# Revit family: S-776
name_source: partatom
category: Aparatos sanitarios
revit_build: Autodesk Revit 2015 (Build: 20140606_1530(x64)
units: mm (PartAtom-declared; Revit-internal decimal feet)

## types (6) — shared parameters
B = 72 mm
Comentarios de tipo = COMPATIBLE CON CERCOS VISTOS Y OCULTOS
Descripción = REJILLA PARA CANALETA, SEQUENCE, PARA CANALETAS ANCHO 70
DistExt = 15 mm  [stored 0.0492126 ft]
Fabricante = Jimten
Material = INOX AISI304
Modelo = S-776
Rejilla = INOX AISI304
URL = http://www.jimten.com

## per-type parameters (varying)
| type | A | Medida | N_MatrizHuecos | Referencia |
| 70x350mm_SEQUENCE | 340 mm | 350mm x 70mm | 3 | 13739 |
| 70x550mm_SEQUENCE | 540 mm  [stored 1.77165 ft] | 550mm x 70mm | 5 | 13759 |
| 70x650mm_SEQUENCE | 640 mm  [stored 2.09974 ft] | 650mm x 70mm | 6 | 13769 |
| 70x750mm_SEQUENCE | 740 mm | 750mm x 70mm | 7 | 13779 |
| 70x850mm_SEQUENCE | 840 mm | 850mm x 70mm | 8 | 13789 |
| 70x950mm_SEQUENCE | 940 mm | 950mm x 70mm | 9 | 13799 |

note: [stored X ft] marks values corroborated as IEEE doubles in the binary element streams (Revit-internal decimal feet)

## geometry (parser evidence)
native form markers: Blend x3, Sweep x2
no freeform markers — native parametric forms only
